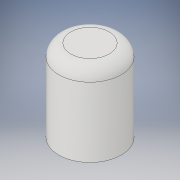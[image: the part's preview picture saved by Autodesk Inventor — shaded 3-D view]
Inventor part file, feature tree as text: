
AUTODESK INVENTOR PART (.ipt)
format: ipt  version: 2018 (Build 220112000, 112)  size: 125,440 bytes
history: native  units: in
note: dims shown in document units (in); Inventor stores cm internally (conversion verified against a paired STEP export)
features: extrude x1, shell x1, fillet x1, sketch x1
ambient origin geometry x8: Origin, YZ Plane, XZ Plane, XY Plane, X Axis, Y Axis, Z Axis, Center Point
bodies: Solid1 (feature_tree)
feature tree (4):
  extrude  "Extrusion1"  Depth=0.425in TaperAngle=0.0deg
  shell  "Shell1"  Thickness=0.025in
  fillet  "Fillet1"  Radius=0.0625in
  sketch  "Sketch1"  dims[d0=0.325in d1=0.425in d2=0.0in d3=0.025in d4=0.0625in]
